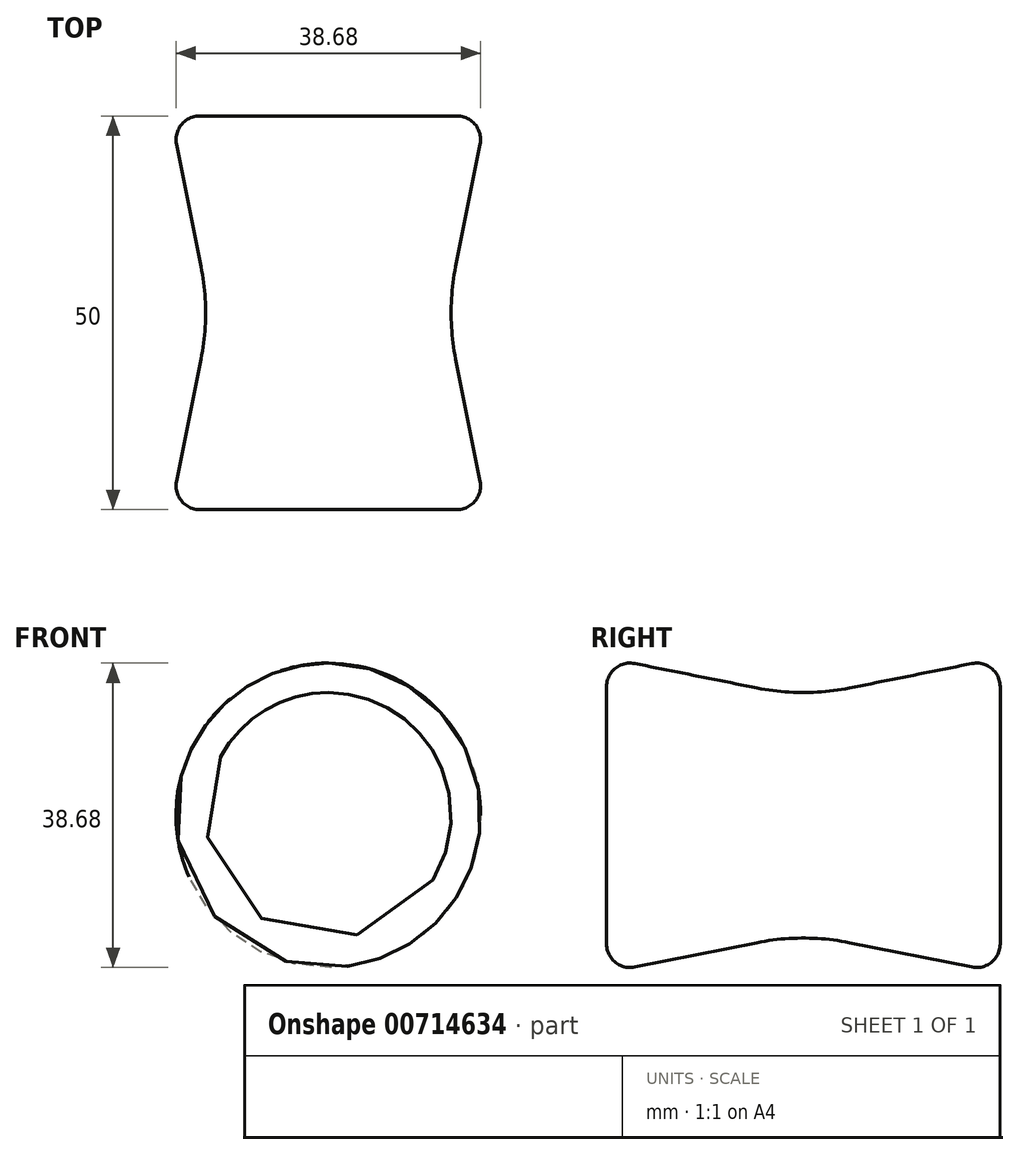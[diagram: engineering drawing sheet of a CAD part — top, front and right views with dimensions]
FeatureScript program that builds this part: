
annotation { "Feature Type Name" : "Feature", "Feature Type Description" : "" }
export const myFeature = defineFeature(function(context is Context, id is Id, definition is map)
    precondition{}
    {
        {
            var Q0;
            Q0=qCreatedBy(makeId("Top.planeOp"),FACE);
            var sketch = newSketch(context, id + "F0", { "sketchPlane" : qUnion([Q0])});
            skLineSegment(sketch, "E0", {"start": v(19.28, 3.59) * mm, "end": v(16.18, 19.12) * mm});
            skLineSegment(sketch, "E1", {"start": v(16.18, 30.88) * mm, "end": v(19.28, 46.41) * mm});
            skLineSegment(sketch, "E2", {"start": v(16.34, 50) * mm, "end": v(0, 50) * mm});
            skLineSegment(sketch, "E3", {"start": v(16.34, 0) * mm, "end": v(0, 0) * mm});
            skLineSegment(sketch, "E4", {"start": v(15, 25) * mm, "end": v(0, 25) * mm});
            skPoint(sketch, "E5.visualSharp", {"position": v(15, 25) * mm});
            skArc(sketch, "E5.filletArc", {"start": v(16.18, 30.88) * mm, "mid": v(15.6, 25) * mm, "end": v(16.18, 19.12) * mm});
            skPoint(sketch, "E6.visualSharp", {"position": v(20, 50) * mm});
            skArc(sketch, "E6.filletArc", {"start": v(19.28, 46.41) * mm, "mid": v(18.66, 48.9) * mm, "end": v(16.34, 50) * mm});
            skPoint(sketch, "E7.visualSharp", {"position": v(20, 0) * mm});
            skArc(sketch, "E7.filletArc", {"start": v(16.34, 0) * mm, "mid": v(18.66, 1.1) * mm, "end": v(19.28, 3.59) * mm});
            skLineSegment(sketch, "E8", {"start": v(0, 0) * mm, "end": v(0, 67.23) * mm, "construction": true});
            skSolve(sketch);
        }
        {
            var Q0;
            Q0=sQuery(id+"F0.wireOp",EDGE,"E2");
            var Q1;
            Q1=sQuery(id+"F0.wireOp",EDGE,"E6.filletArc");
            var Q2;
            Q2=sQuery(id+"F0.wireOp",EDGE,"E1");
            var Q3;
            Q3=sQuery(id+"F0.wireOp",EDGE,"E5.filletArc");
            var Q4;
            Q4=sQuery(id+"F0.wireOp",EDGE,"E0");
            var Q5;
            Q5=sQuery(id+"F0.wireOp",EDGE,"E7.filletArc");
            var Q6;
            Q6=sQuery(id+"F0.wireOp",EDGE,"E3");
            var Q7;
            Q7=sQuery(id+"F0.wireOp",EDGE,"E8");
            revolve(context, id + "F1", {"bodyType" : ToolBodyType.SURFACE, "surfaceOperationType" : NewSurfaceOperationType.NEW, "surfaceEntities" : qUnion([Q0, Q1, Q2, Q3, Q4, Q5, Q6]), "axis" : qUnion([Q7]), "revolveType" : RevolveType.FULL});
        }
    });
